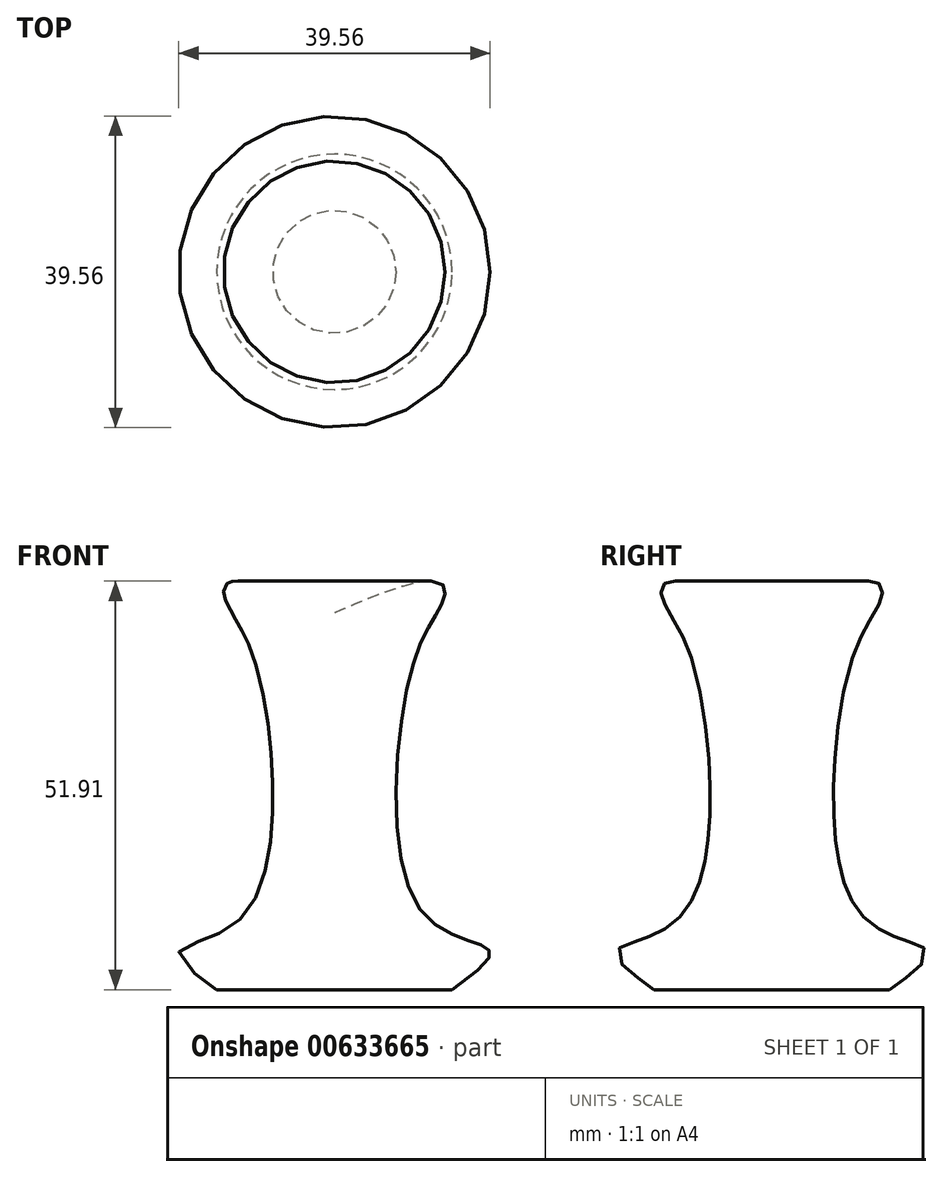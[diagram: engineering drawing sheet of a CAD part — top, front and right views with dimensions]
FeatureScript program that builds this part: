
annotation { "Feature Type Name" : "Feature", "Feature Type Description" : "" }
export const myFeature = defineFeature(function(context is Context, id is Id, definition is map)
    precondition{}
    {
        {
            var Q0;
            Q0=qCreatedBy(makeId("Front.planeOp"),FACE);
            var sketch = newSketch(context, id + "F0", { "sketchPlane" : qUnion([Q0])});
            skFitSpline(sketch, "E0", {"points": [v(0, 0) * mm, v(10.17, 0) * mm, v(14.95, 0) * mm], "startDerivative": vector(28.6, 0) * mm, "endDerivative": vector(2.69, 0) * mm});
            skFitSpline(sketch, "E1", {"points": [v(14.95, 0) * mm, v(19, 5.48) * mm, v(10.6, 10.58) * mm, v(10.07, 41.6) * mm, v(13.67, 49.1) * mm, v(0, 47.82) * mm], "startDerivative": vector(109.28, 75.07) * mm, "endDerivative": vector(-213.46, -96.75) * mm});
            skFitSpline(sketch, "E2", {"points": [v(0, 47.82) * mm, v(0, 0) * mm], "startDerivative": vector(0, -48.68) * mm, "endDerivative": vector(0, -48.68) * mm});
            skLineSegment(sketch, "E3", {"start": v(0, 54.75) * mm, "end": v(0, -10.67) * mm, "construction": true});
            skSolve(sketch);
        }
        {
            var Q0;
            Q0=makeQuery(id+"F0.imprint","IMPRINT",FACE,{"disambiguationData":[TD([[makeQuery(id+"F0.imprint","IMPRINT",EDGE,{"derivedFrom":sQuery(id+"F0.wireOp",EDGE,"E0")}),1.0]])]});
            var Q1;
            Q1 = qConstructionFilter(qBodyType(qCreatedBy(id + "F0" ,EDGE), BodyType.WIRE), ConstructionObject.NO);
            var Q2;
            Q2=sQuery(id+"F0.wireOp",EDGE,"E3");
            revolve(context, id + "F1", {"entities" : qUnion([Q0]), "surfaceEntities" : qUnion([Q1]), "axis" : qUnion([Q2]), "revolveType" : RevolveType.FULL});
        }
    });
